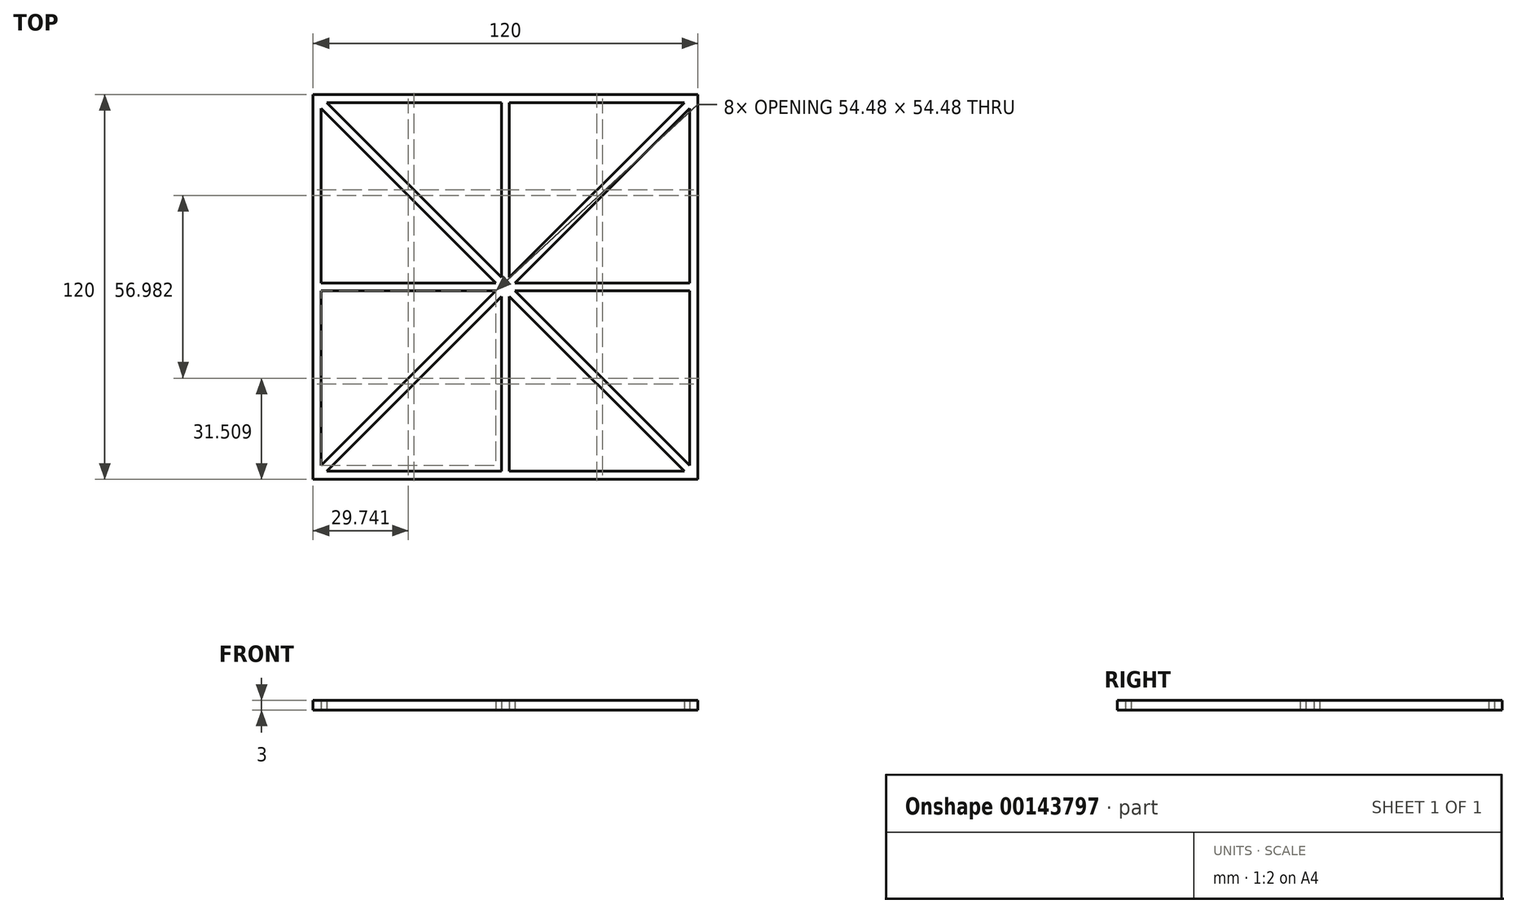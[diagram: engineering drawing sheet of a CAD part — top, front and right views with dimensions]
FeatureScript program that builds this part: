
annotation { "Feature Type Name" : "Feature", "Feature Type Description" : "" }
export const myFeature = defineFeature(function(context is Context, id is Id, definition is map)
    precondition{}
    {
        {
            var Q0;
            Q0=qCreatedBy(makeId("Top.planeOp"),FACE);
            var sketch = newSketch(context, id + "F0", { "sketchPlane" : qUnion([Q0])});
            skLineSegment(sketch, "E0.bottom", {"start": v(-60, 60) * mm, "end": v(60, 60) * mm});
            skLineSegment(sketch, "E0.top", {"start": v(-60, -60) * mm, "end": v(60, -60) * mm});
            skLineSegment(sketch, "E0.left", {"start": v(-60, 60) * mm, "end": v(-60, -60) * mm});
            skLineSegment(sketch, "E0.right", {"start": v(60, 60) * mm, "end": v(60, -60) * mm});
            skPoint(sketch, "E0.middle", {"position": v(0, 0) * mm});
            skLineSegment(sketch, "E1.bottom", {"start": v(-57.5, 57.5) * mm, "end": v(57.5, 57.5) * mm});
            skLineSegment(sketch, "E1.top", {"start": v(-57.5, -57.5) * mm, "end": v(57.5, -57.5) * mm});
            skLineSegment(sketch, "E1.left", {"start": v(-57.5, 57.5) * mm, "end": v(-57.5, -57.5) * mm});
            skLineSegment(sketch, "E1.right", {"start": v(57.5, 57.5) * mm, "end": v(57.5, -57.5) * mm});
            skLineSegment(sketch, "E2", {"start": v(60, 60) * mm, "end": v(-60, -60) * mm});
            skLineSegment(sketch, "E3", {"start": v(-60, 60) * mm, "end": v(60, -60) * mm});
            skLineSegment(sketch, "E4", {"start": v(-58.23, 60) * mm, "end": v(60, -58.23) * mm});
            skLineSegment(sketch, "E5.MirrorCS", {"start": v(-60, 58.23) * mm, "end": v(58.23, -60) * mm});
            skLineSegment(sketch, "E6", {"start": v(58.23, 60) * mm, "end": v(-60, -58.23) * mm});
            skLineSegment(sketch, "E7.MirrorCS", {"start": v(60, 58.23) * mm, "end": v(-58.23, -60) * mm});
            skLineSegment(sketch, "E8", {"start": v(-1.25, -57.5) * mm, "end": v(-1.25, 57.5) * mm});
            skLineSegment(sketch, "E9", {"start": v(-57.5, -1.25) * mm, "end": v(57.5, -1.25) * mm});
            skLineSegment(sketch, "E10.MirrorCS", {"start": v(1.25, -57.5) * mm, "end": v(1.25, 57.5) * mm});
            skLineSegment(sketch, "E11.MirrorCS", {"start": v(-57.5, 1.25) * mm, "end": v(57.5, 1.25) * mm});
            skSolve(sketch);
        }
        {
            var Q0;
            {var subQ1=sQuery(id+"F0.wireOp",EDGE,"E1.bottom");var subQ3=sQuery(id+"F0.wireOp",EDGE,"E6");var subQ4=makeQuery(id+"F0.imprint","INTERSECT",VERTEX,{"derivedFrom":[subQ1,subQ3]});Q0=makeQuery(id+"F0.imprint","IMPRINT",FACE,{"disambiguationData":[TD([[makeQuery(id+"F0.imprint","IMPRINT",EDGE,{"disambiguationData":[TD([[subQ4,-1.0]])],"derivedFrom":subQ3}),1.0]])]});}
            var Q1;
            {var subQ5=sQuery(id+"F0.wireOp",EDGE,"E5.MirrorCS");var subQ7=sQuery(id+"F0.wireOp",EDGE,"E0.top");var subQ8=makeQuery(id+"F0.imprint","INTERSECT",VERTEX,{"derivedFrom":[subQ7,subQ5]});Q1=makeQuery(id+"F0.imprint","IMPRINT",FACE,{"disambiguationData":[TD([[makeQuery(id+"F0.imprint","IMPRINT",EDGE,{"disambiguationData":[TD([[subQ8,1.0]])],"derivedFrom":subQ7}),1.0]])]});}
            var Q2;
            {var subQ5=sQuery(id+"F0.wireOp",EDGE,"E9");var subQ6=sQuery(id+"F0.wireOp",EDGE,"E1.right");var subQ7=makeQuery(id+"F0.imprint","INTERSECT",VERTEX,{"derivedFrom":[subQ6,subQ5]});Q2=makeQuery(id+"F0.imprint","IMPRINT",FACE,{"disambiguationData":[TD([[makeQuery(id+"F0.imprint","IMPRINT",EDGE,{"disambiguationData":[TD([[subQ7,1.0]])],"derivedFrom":subQ6}),-1.0]])]});}
            var Q3;
            {var subQ0=sQuery(id+"F0.wireOp",EDGE,"E8");var subQ1=sQuery(id+"F0.wireOp",EDGE,"E1.bottom");var subQ2=makeQuery(id+"F0.imprint","INTERSECT",VERTEX,{"derivedFrom":[subQ1,subQ0]});Q3=makeQuery(id+"F0.imprint","IMPRINT",FACE,{"disambiguationData":[TD([[makeQuery(id+"F0.imprint","IMPRINT",EDGE,{"disambiguationData":[TD([[subQ2,-1.0]])],"derivedFrom":subQ1}),-1.0]])]});}
            var Q4;
            {var subQ1=sQuery(id+"F0.wireOp",EDGE,"E1.left");var subQ3=sQuery(id+"F0.wireOp",EDGE,"E5.MirrorCS");var subQ4=makeQuery(id+"F0.imprint","INTERSECT",VERTEX,{"derivedFrom":[subQ1,subQ3]});Q4=makeQuery(id+"F0.imprint","IMPRINT",FACE,{"disambiguationData":[TD([[makeQuery(id+"F0.imprint","IMPRINT",EDGE,{"disambiguationData":[TD([[subQ4,-1.0]])],"derivedFrom":subQ3}),1.0]])]});}
            var Q5;
            {var subQ4=sQuery(id+"F0.wireOp",EDGE,"E5.MirrorCS");var subQ5=sQuery(id+"F0.wireOp",EDGE,"E0.left");var subQ6=makeQuery(id+"F0.imprint","INTERSECT",VERTEX,{"derivedFrom":[subQ5,subQ4]});Q5=makeQuery(id+"F0.imprint","IMPRINT",FACE,{"disambiguationData":[TD([[makeQuery(id+"F0.imprint","IMPRINT",EDGE,{"disambiguationData":[TD([[subQ6,-1.0]])],"derivedFrom":subQ5}),1.0]])]});}
            var Q6;
            {var subQ1=sQuery(id+"F0.wireOp",EDGE,"E1.top");var subQ3=sQuery(id+"F0.wireOp",EDGE,"E7.MirrorCS");var subQ4=makeQuery(id+"F0.imprint","INTERSECT",VERTEX,{"derivedFrom":[subQ1,subQ3]});Q6=makeQuery(id+"F0.imprint","IMPRINT",FACE,{"disambiguationData":[TD([[makeQuery(id+"F0.imprint","IMPRINT",EDGE,{"disambiguationData":[TD([[subQ4,1.0]])],"derivedFrom":subQ3}),-1.0]])]});}
            var Q7;
            {var subQ0=sQuery(id+"F0.wireOp",EDGE,"E8");var subQ1=sQuery(id+"F0.wireOp",EDGE,"E1.top");var subQ2=makeQuery(id+"F0.imprint","INTERSECT",VERTEX,{"derivedFrom":[subQ1,subQ0]});Q7=makeQuery(id+"F0.imprint","IMPRINT",FACE,{"disambiguationData":[TD([[makeQuery(id+"F0.imprint","IMPRINT",EDGE,{"disambiguationData":[TD([[subQ2,-1.0]])],"derivedFrom":subQ1}),1.0]])]});}
            var Q8;
            {var subQ1=sQuery(id+"F0.wireOp",EDGE,"E1.left");var subQ3=sQuery(id+"F0.wireOp",EDGE,"E6");var subQ4=makeQuery(id+"F0.imprint","INTERSECT",VERTEX,{"derivedFrom":[subQ1,subQ3]});Q8=makeQuery(id+"F0.imprint","IMPRINT",FACE,{"disambiguationData":[TD([[makeQuery(id+"F0.imprint","IMPRINT",EDGE,{"disambiguationData":[TD([[subQ4,1.0]])],"derivedFrom":subQ3}),1.0]])]});}
            var Q9;
            {var subQ5=sQuery(id+"F0.wireOp",EDGE,"E4");var subQ7=sQuery(id+"F0.wireOp",EDGE,"E0.bottom");var subQ8=makeQuery(id+"F0.imprint","INTERSECT",VERTEX,{"derivedFrom":[subQ7,subQ5]});Q9=makeQuery(id+"F0.imprint","IMPRINT",FACE,{"disambiguationData":[TD([[makeQuery(id+"F0.imprint","IMPRINT",EDGE,{"disambiguationData":[TD([[subQ8,-1.0]])],"derivedFrom":subQ7}),-1.0]])]});}
            var Q10;
            {var subQ3=sQuery(id+"F0.wireOp",EDGE,"E9");var subQ5=sQuery(id+"F0.wireOp",EDGE,"E1.left");var subQ6=makeQuery(id+"F0.imprint","INTERSECT",VERTEX,{"derivedFrom":[subQ5,subQ3]});Q10=makeQuery(id+"F0.imprint","IMPRINT",FACE,{"disambiguationData":[TD([[makeQuery(id+"F0.imprint","IMPRINT",EDGE,{"disambiguationData":[TD([[subQ6,1.0]])],"derivedFrom":subQ5}),1.0]])]});}
            var Q11;
            {var subQ1=sQuery(id+"F0.wireOp",EDGE,"E1.right");var subQ3=sQuery(id+"F0.wireOp",EDGE,"E7.MirrorCS");var subQ4=makeQuery(id+"F0.imprint","INTERSECT",VERTEX,{"derivedFrom":[subQ1,subQ3]});Q11=makeQuery(id+"F0.imprint","IMPRINT",FACE,{"disambiguationData":[TD([[makeQuery(id+"F0.imprint","IMPRINT",EDGE,{"disambiguationData":[TD([[subQ4,-1.0]])],"derivedFrom":subQ3}),-1.0]])]});}
            var Q12;
            {var subQ2=sQuery(id+"F0.wireOp",EDGE,"E4");var subQ4=sQuery(id+"F0.wireOp",EDGE,"E0.right");var subQ5=makeQuery(id+"F0.imprint","INTERSECT",VERTEX,{"derivedFrom":[subQ4,subQ2]});Q12=makeQuery(id+"F0.imprint","IMPRINT",FACE,{"disambiguationData":[TD([[makeQuery(id+"F0.imprint","IMPRINT",EDGE,{"disambiguationData":[TD([[subQ5,1.0]])],"derivedFrom":subQ4}),-1.0]])]});}
            var Q13;
            {var subQ0=sQuery(id+"F0.wireOp",EDGE,"E10.MirrorCS");var subQ1=sQuery(id+"F0.wireOp",EDGE,"E4");var subQ2=makeQuery(id+"F0.imprint","INTERSECT",VERTEX,{"derivedFrom":[subQ1,subQ0]});Q13=makeQuery(id+"F0.imprint","IMPRINT",FACE,{"disambiguationData":[TD([[makeQuery(id+"F0.imprint","IMPRINT",EDGE,{"disambiguationData":[TD([[subQ2,-1.0]])],"derivedFrom":subQ1}),1.0]])]});}
            var Q14;
            {var subQ1=sQuery(id+"F0.wireOp",EDGE,"E1.right");var subQ3=sQuery(id+"F0.wireOp",EDGE,"E4");var subQ4=makeQuery(id+"F0.imprint","INTERSECT",VERTEX,{"derivedFrom":[subQ1,subQ3]});Q14=makeQuery(id+"F0.imprint","IMPRINT",FACE,{"disambiguationData":[TD([[makeQuery(id+"F0.imprint","IMPRINT",EDGE,{"disambiguationData":[TD([[subQ4,1.0]])],"derivedFrom":subQ3}),-1.0]])]});}
            var Q15;
            {var subQ0=sQuery(id+"F0.wireOp",EDGE,"E8");var subQ1=sQuery(id+"F0.wireOp",EDGE,"E4");var subQ2=makeQuery(id+"F0.imprint","INTERSECT",VERTEX,{"derivedFrom":[subQ1,subQ0]});Q15=makeQuery(id+"F0.imprint","IMPRINT",FACE,{"disambiguationData":[TD([[makeQuery(id+"F0.imprint","IMPRINT",EDGE,{"disambiguationData":[TD([[subQ2,-1.0]])],"derivedFrom":subQ1}),-1.0]])]});}
            var Q16;
            {var subQ0=sQuery(id+"F0.wireOp",EDGE,"E9");var subQ1=sQuery(id+"F0.wireOp",EDGE,"E5.MirrorCS");var subQ2=makeQuery(id+"F0.imprint","INTERSECT",VERTEX,{"derivedFrom":[subQ1,subQ0]});Q16=makeQuery(id+"F0.imprint","IMPRINT",FACE,{"disambiguationData":[TD([[makeQuery(id+"F0.imprint","IMPRINT",EDGE,{"disambiguationData":[TD([[subQ2,-1.0]])],"derivedFrom":subQ1}),-1.0]])]});}
            var Q17;
            {var subQ1=sQuery(id+"F0.wireOp",EDGE,"E0.bottom");var subQ3=sQuery(id+"F0.wireOp",EDGE,"E4");var subQ4=makeQuery(id+"F0.imprint","INTERSECT",VERTEX,{"derivedFrom":[subQ1,subQ3]});Q17=makeQuery(id+"F0.imprint","IMPRINT",FACE,{"disambiguationData":[TD([[makeQuery(id+"F0.imprint","IMPRINT",EDGE,{"disambiguationData":[TD([[subQ4,-1.0]])],"derivedFrom":subQ3}),-1.0]])]});}
            var Q18;
            {var subQ1=sQuery(id+"F0.wireOp",EDGE,"E0.bottom");var subQ3=sQuery(id+"F0.wireOp",EDGE,"E6");var subQ4=makeQuery(id+"F0.imprint","INTERSECT",VERTEX,{"derivedFrom":[subQ1,subQ3]});Q18=makeQuery(id+"F0.imprint","IMPRINT",FACE,{"disambiguationData":[TD([[makeQuery(id+"F0.imprint","IMPRINT",EDGE,{"disambiguationData":[TD([[subQ4,-1.0]])],"derivedFrom":subQ3}),1.0]])]});}
            var Q19;
            {var subQ1=sQuery(id+"F0.wireOp",EDGE,"E0.top");var subQ3=sQuery(id+"F0.wireOp",EDGE,"E7.MirrorCS");var subQ4=makeQuery(id+"F0.imprint","INTERSECT",VERTEX,{"derivedFrom":[subQ1,subQ3]});Q19=makeQuery(id+"F0.imprint","IMPRINT",FACE,{"disambiguationData":[TD([[makeQuery(id+"F0.imprint","IMPRINT",EDGE,{"disambiguationData":[TD([[subQ4,1.0]])],"derivedFrom":subQ3}),-1.0]])]});}
            var Q20;
            {var subQ1=sQuery(id+"F0.wireOp",EDGE,"E0.top");var subQ3=sQuery(id+"F0.wireOp",EDGE,"E5.MirrorCS");var subQ4=makeQuery(id+"F0.imprint","INTERSECT",VERTEX,{"derivedFrom":[subQ1,subQ3]});Q20=makeQuery(id+"F0.imprint","IMPRINT",FACE,{"disambiguationData":[TD([[makeQuery(id+"F0.imprint","IMPRINT",EDGE,{"disambiguationData":[TD([[subQ4,1.0]])],"derivedFrom":subQ3}),1.0]])]});}
            var Q21;
            {var subQ1=sQuery(id+"F0.wireOp",EDGE,"E0.left");var subQ3=sQuery(id+"F0.wireOp",EDGE,"E5.MirrorCS");var subQ4=makeQuery(id+"F0.imprint","INTERSECT",VERTEX,{"derivedFrom":[subQ1,subQ3]});Q21=makeQuery(id+"F0.imprint","IMPRINT",FACE,{"disambiguationData":[TD([[makeQuery(id+"F0.imprint","IMPRINT",EDGE,{"disambiguationData":[TD([[subQ4,-1.0]])],"derivedFrom":subQ3}),1.0]])]});}
            var Q22;
            {var subQ1=sQuery(id+"F0.wireOp",EDGE,"E0.left");var subQ3=sQuery(id+"F0.wireOp",EDGE,"E6");var subQ4=makeQuery(id+"F0.imprint","INTERSECT",VERTEX,{"derivedFrom":[subQ1,subQ3]});Q22=makeQuery(id+"F0.imprint","IMPRINT",FACE,{"disambiguationData":[TD([[makeQuery(id+"F0.imprint","IMPRINT",EDGE,{"disambiguationData":[TD([[subQ4,1.0]])],"derivedFrom":subQ3}),1.0]])]});}
            var Q23;
            {var subQ1=sQuery(id+"F0.wireOp",EDGE,"E0.right");var subQ3=sQuery(id+"F0.wireOp",EDGE,"E4");var subQ4=makeQuery(id+"F0.imprint","INTERSECT",VERTEX,{"derivedFrom":[subQ1,subQ3]});Q23=makeQuery(id+"F0.imprint","IMPRINT",FACE,{"disambiguationData":[TD([[makeQuery(id+"F0.imprint","IMPRINT",EDGE,{"disambiguationData":[TD([[subQ4,1.0]])],"derivedFrom":subQ3}),-1.0]])]});}
            var Q24;
            {var subQ0=sQuery(id+"F0.wireOp",EDGE,"E7.MirrorCS");var subQ1=sQuery(id+"F0.wireOp",EDGE,"E5.MirrorCS");var subQ2=makeQuery(id+"F0.imprint","INTERSECT",VERTEX,{"derivedFrom":[subQ1,subQ0]});Q24=makeQuery(id+"F0.imprint","IMPRINT",FACE,{"disambiguationData":[TD([[makeQuery(id+"F0.imprint","IMPRINT",EDGE,{"disambiguationData":[TD([[subQ2,-1.0]])],"derivedFrom":subQ1}),1.0]])]});}
            var Q25;
            {var subQ0=sQuery(id+"F0.wireOp",EDGE,"E7.MirrorCS");var subQ1=sQuery(id+"F0.wireOp",EDGE,"E4");var subQ2=makeQuery(id+"F0.imprint","INTERSECT",VERTEX,{"derivedFrom":[subQ1,subQ0]});Q25=makeQuery(id+"F0.imprint","IMPRINT",FACE,{"disambiguationData":[TD([[makeQuery(id+"F0.imprint","IMPRINT",EDGE,{"disambiguationData":[TD([[subQ2,-1.0]])],"derivedFrom":subQ1}),-1.0]])]});}
            var Q26;
            {var subQ0=sQuery(id+"F0.wireOp",EDGE,"E6");var subQ1=sQuery(id+"F0.wireOp",EDGE,"E4");var subQ2=makeQuery(id+"F0.imprint","INTERSECT",VERTEX,{"derivedFrom":[subQ1,subQ0]});Q26=makeQuery(id+"F0.imprint","IMPRINT",FACE,{"disambiguationData":[TD([[makeQuery(id+"F0.imprint","IMPRINT",EDGE,{"disambiguationData":[TD([[subQ2,-1.0]])],"derivedFrom":subQ1}),1.0]])]});}
            var Q27;
            {var subQ1=sQuery(id+"F0.wireOp",EDGE,"E1.bottom");var subQ3=sQuery(id+"F0.wireOp",EDGE,"E4");var subQ4=makeQuery(id+"F0.imprint","INTERSECT",VERTEX,{"derivedFrom":[subQ1,subQ3]});Q27=makeQuery(id+"F0.imprint","IMPRINT",FACE,{"disambiguationData":[TD([[makeQuery(id+"F0.imprint","IMPRINT",EDGE,{"disambiguationData":[TD([[subQ4,-1.0]])],"derivedFrom":subQ3}),-1.0]])]});}
            var Q28;
            {var subQ0=sQuery(id+"F0.wireOp",EDGE,"E11.MirrorCS");var subQ1=sQuery(id+"F0.wireOp",EDGE,"E5.MirrorCS");var subQ2=makeQuery(id+"F0.imprint","INTERSECT",VERTEX,{"derivedFrom":[subQ1,subQ0]});Q28=makeQuery(id+"F0.imprint","IMPRINT",FACE,{"disambiguationData":[TD([[makeQuery(id+"F0.imprint","IMPRINT",EDGE,{"disambiguationData":[TD([[subQ2,-1.0]])],"derivedFrom":subQ1}),1.0]])]});}
            var Q29;
            {var subQ1=sQuery(id+"F0.wireOp",EDGE,"E1.top");var subQ3=sQuery(id+"F0.wireOp",EDGE,"E5.MirrorCS");var subQ4=makeQuery(id+"F0.imprint","INTERSECT",VERTEX,{"derivedFrom":[subQ1,subQ3]});Q29=makeQuery(id+"F0.imprint","IMPRINT",FACE,{"disambiguationData":[TD([[makeQuery(id+"F0.imprint","IMPRINT",EDGE,{"disambiguationData":[TD([[subQ4,1.0]])],"derivedFrom":subQ3}),1.0]])]});}
            var Q30;
            {var subQ0=sQuery(id+"F0.wireOp",EDGE,"E6");var subQ1=sQuery(id+"F0.wireOp",EDGE,"E5.MirrorCS");var subQ2=makeQuery(id+"F0.imprint","INTERSECT",VERTEX,{"derivedFrom":[subQ1,subQ0]});Q30=makeQuery(id+"F0.imprint","IMPRINT",FACE,{"disambiguationData":[TD([[makeQuery(id+"F0.imprint","IMPRINT",EDGE,{"disambiguationData":[TD([[subQ2,-1.0]])],"derivedFrom":subQ1}),-1.0]])]});}
            var Q31;
            {var subQ1=sQuery(id+"F0.wireOp",EDGE,"E2");var subQ6=sQuery(id+"F0.wireOp",EDGE,"E3");var subQ9=makeQuery(id+"F0.imprint","INTERSECT",VERTEX,{"derivedFrom":[subQ1,subQ6]});Q31=makeQuery(id+"F0.imprint","IMPRINT",FACE,{"disambiguationData":[TD([[makeQuery(id+"F0.imprint","IMPRINT",EDGE,{"disambiguationData":[TD([[subQ9,-1.0]])],"derivedFrom":subQ1}),-1.0]])]});}
            var Q32;
            {var subQ5=sQuery(id+"F0.wireOp",EDGE,"E2");var subQ7=sQuery(id+"F0.wireOp",EDGE,"E4");var subQ8=makeQuery(id+"F0.imprint","INTERSECT",VERTEX,{"derivedFrom":[subQ5,subQ7]});Q32=makeQuery(id+"F0.imprint","IMPRINT",FACE,{"disambiguationData":[TD([[makeQuery(id+"F0.imprint","IMPRINT",EDGE,{"disambiguationData":[TD([[subQ8,-1.0]])],"derivedFrom":subQ5}),-1.0]])]});}
            var Q33;
            {var subQ0=sQuery(id+"F0.wireOp",EDGE,"E5.MirrorCS");var subQ1=sQuery(id+"F0.wireOp",EDGE,"E2");var subQ2=makeQuery(id+"F0.imprint","INTERSECT",VERTEX,{"derivedFrom":[subQ1,subQ0]});Q33=makeQuery(id+"F0.imprint","IMPRINT",FACE,{"disambiguationData":[TD([[makeQuery(id+"F0.imprint","IMPRINT",EDGE,{"disambiguationData":[TD([[subQ2,-1.0]])],"derivedFrom":subQ0}),-1.0]])]});}
            var Q34;
            {var subQ0=sQuery(id+"F0.wireOp",EDGE,"E6");var subQ1=sQuery(id+"F0.wireOp",EDGE,"E5.MirrorCS");var subQ2=makeQuery(id+"F0.imprint","INTERSECT",VERTEX,{"derivedFrom":[subQ1,subQ0]});Q34=makeQuery(id+"F0.imprint","IMPRINT",FACE,{"disambiguationData":[TD([[makeQuery(id+"F0.imprint","IMPRINT",EDGE,{"disambiguationData":[TD([[subQ2,-1.0]])],"derivedFrom":subQ1}),1.0]])]});}
            var Q35;
            {var subQ0=sQuery(id+"F0.wireOp",EDGE,"E6");var subQ1=sQuery(id+"F0.wireOp",EDGE,"E3");var subQ2=makeQuery(id+"F0.imprint","INTERSECT",VERTEX,{"derivedFrom":[subQ1,subQ0]});Q35=makeQuery(id+"F0.imprint","IMPRINT",FACE,{"disambiguationData":[TD([[makeQuery(id+"F0.imprint","IMPRINT",EDGE,{"disambiguationData":[TD([[subQ2,1.0]])],"derivedFrom":subQ0}),-1.0]])]});}
            var Q36;
            {var subQ0=sQuery(id+"F0.wireOp",EDGE,"E7.MirrorCS");var subQ1=sQuery(id+"F0.wireOp",EDGE,"E3");var subQ2=makeQuery(id+"F0.imprint","INTERSECT",VERTEX,{"derivedFrom":[subQ1,subQ0]});Q36=makeQuery(id+"F0.imprint","IMPRINT",FACE,{"disambiguationData":[TD([[makeQuery(id+"F0.imprint","IMPRINT",EDGE,{"disambiguationData":[TD([[subQ2,1.0]])],"derivedFrom":subQ0}),1.0]])]});}
            var Q37;
            {var subQ0=sQuery(id+"F0.wireOp",EDGE,"E4");var subQ1=sQuery(id+"F0.wireOp",EDGE,"E2");var subQ2=makeQuery(id+"F0.imprint","INTERSECT",VERTEX,{"derivedFrom":[subQ1,subQ0]});Q37=makeQuery(id+"F0.imprint","IMPRINT",FACE,{"disambiguationData":[TD([[makeQuery(id+"F0.imprint","IMPRINT",EDGE,{"disambiguationData":[TD([[subQ2,1.0]])],"derivedFrom":subQ0}),1.0]])]});}
            var Q38;
            {var subQ1=sQuery(id+"F0.wireOp",EDGE,"E0.right");var subQ3=sQuery(id+"F0.wireOp",EDGE,"E7.MirrorCS");var subQ4=makeQuery(id+"F0.imprint","INTERSECT",VERTEX,{"derivedFrom":[subQ1,subQ3]});Q38=makeQuery(id+"F0.imprint","IMPRINT",FACE,{"disambiguationData":[TD([[makeQuery(id+"F0.imprint","IMPRINT",EDGE,{"disambiguationData":[TD([[subQ4,-1.0]])],"derivedFrom":subQ3}),-1.0]])]});}
            var Q39;
            {var subQ0=sQuery(id+"F0.wireOp",EDGE,"E9");var subQ1=sQuery(id+"F0.wireOp",EDGE,"E5.MirrorCS");var subQ2=makeQuery(id+"F0.imprint","INTERSECT",VERTEX,{"derivedFrom":[subQ1,subQ0]});Q39=makeQuery(id+"F0.imprint","IMPRINT",FACE,{"disambiguationData":[TD([[makeQuery(id+"F0.imprint","IMPRINT",EDGE,{"disambiguationData":[TD([[subQ2,-1.0]])],"derivedFrom":subQ1}),1.0]])]});}
            var Q40;
            {var subQ1=sQuery(id+"F0.wireOp",EDGE,"E3");var subQ6=sQuery(id+"F0.wireOp",EDGE,"E2");var subQ9=makeQuery(id+"F0.imprint","INTERSECT",VERTEX,{"derivedFrom":[subQ6,subQ1]});Q40=makeQuery(id+"F0.imprint","IMPRINT",FACE,{"disambiguationData":[TD([[makeQuery(id+"F0.imprint","IMPRINT",EDGE,{"disambiguationData":[TD([[subQ9,-1.0]])],"derivedFrom":subQ6}),1.0]])]});}
            var Q41;
            {var subQ0=sQuery(id+"F0.wireOp",EDGE,"E4");var subQ1=sQuery(id+"F0.wireOp",EDGE,"E2");var subQ2=makeQuery(id+"F0.imprint","INTERSECT",VERTEX,{"derivedFrom":[subQ1,subQ0]});Q41=makeQuery(id+"F0.imprint","IMPRINT",FACE,{"disambiguationData":[TD([[makeQuery(id+"F0.imprint","IMPRINT",EDGE,{"disambiguationData":[TD([[subQ2,-1.0]])],"derivedFrom":subQ1}),1.0]])]});}
            var Q42;
            {var subQ0=sQuery(id+"F0.wireOp",EDGE,"E6");var subQ1=sQuery(id+"F0.wireOp",EDGE,"E4");var subQ2=makeQuery(id+"F0.imprint","INTERSECT",VERTEX,{"derivedFrom":[subQ1,subQ0]});Q42=makeQuery(id+"F0.imprint","IMPRINT",FACE,{"disambiguationData":[TD([[makeQuery(id+"F0.imprint","IMPRINT",EDGE,{"disambiguationData":[TD([[subQ2,-1.0]])],"derivedFrom":subQ1}),-1.0]])]});}
            var Q43;
            {var subQ0=sQuery(id+"F0.wireOp",EDGE,"E10.MirrorCS");var subQ1=sQuery(id+"F0.wireOp",EDGE,"E4");var subQ2=makeQuery(id+"F0.imprint","INTERSECT",VERTEX,{"derivedFrom":[subQ1,subQ0]});Q43=makeQuery(id+"F0.imprint","IMPRINT",FACE,{"disambiguationData":[TD([[makeQuery(id+"F0.imprint","IMPRINT",EDGE,{"disambiguationData":[TD([[subQ2,-1.0]])],"derivedFrom":subQ1}),-1.0]])]});}
            var Q44;
            {var subQ0=sQuery(id+"F0.wireOp",EDGE,"E7.MirrorCS");var subQ1=sQuery(id+"F0.wireOp",EDGE,"E3");var subQ2=makeQuery(id+"F0.imprint","INTERSECT",VERTEX,{"derivedFrom":[subQ1,subQ0]});Q44=makeQuery(id+"F0.imprint","IMPRINT",FACE,{"disambiguationData":[TD([[makeQuery(id+"F0.imprint","IMPRINT",EDGE,{"disambiguationData":[TD([[subQ2,-1.0]])],"derivedFrom":subQ0}),1.0]])]});}
            var Q45;
            {var subQ0=sQuery(id+"F0.wireOp",EDGE,"E6");var subQ1=sQuery(id+"F0.wireOp",EDGE,"E3");var subQ2=makeQuery(id+"F0.imprint","INTERSECT",VERTEX,{"derivedFrom":[subQ1,subQ0]});Q45=makeQuery(id+"F0.imprint","IMPRINT",FACE,{"disambiguationData":[TD([[makeQuery(id+"F0.imprint","IMPRINT",EDGE,{"disambiguationData":[TD([[subQ2,-1.0]])],"derivedFrom":subQ0}),-1.0]])]});}
            var Q46;
            {var subQ0=sQuery(id+"F0.wireOp",EDGE,"E4");var subQ1=sQuery(id+"F0.wireOp",EDGE,"E2");var subQ2=makeQuery(id+"F0.imprint","INTERSECT",VERTEX,{"derivedFrom":[subQ1,subQ0]});Q46=makeQuery(id+"F0.imprint","IMPRINT",FACE,{"disambiguationData":[TD([[makeQuery(id+"F0.imprint","IMPRINT",EDGE,{"disambiguationData":[TD([[subQ2,-1.0]])],"derivedFrom":subQ0}),1.0]])]});}
            var Q47;
            {var subQ0=sQuery(id+"F0.wireOp",EDGE,"E5.MirrorCS");var subQ1=sQuery(id+"F0.wireOp",EDGE,"E2");var subQ2=makeQuery(id+"F0.imprint","INTERSECT",VERTEX,{"derivedFrom":[subQ1,subQ0]});Q47=makeQuery(id+"F0.imprint","IMPRINT",FACE,{"disambiguationData":[TD([[makeQuery(id+"F0.imprint","IMPRINT",EDGE,{"disambiguationData":[TD([[subQ2,1.0]])],"derivedFrom":subQ0}),-1.0]])]});}
            extrude(context, id + "F1", {"entities" : qUnion([Q0, Q1, Q2, Q3, Q4, Q5, Q6, Q7, Q8, Q9, Q10, Q11, Q12, Q13, Q14, Q15, Q16, Q17, Q18, Q19, Q20, Q21, Q22, Q23, Q24, Q25, Q26, Q27, Q28, Q29, Q30, Q31, Q32, Q33, Q34, Q35, Q36, Q37, Q38, Q39, Q40, Q41, Q42, Q43, Q44, Q45, Q46, Q47]), "depth" : 3 * mm});
        }
    });
